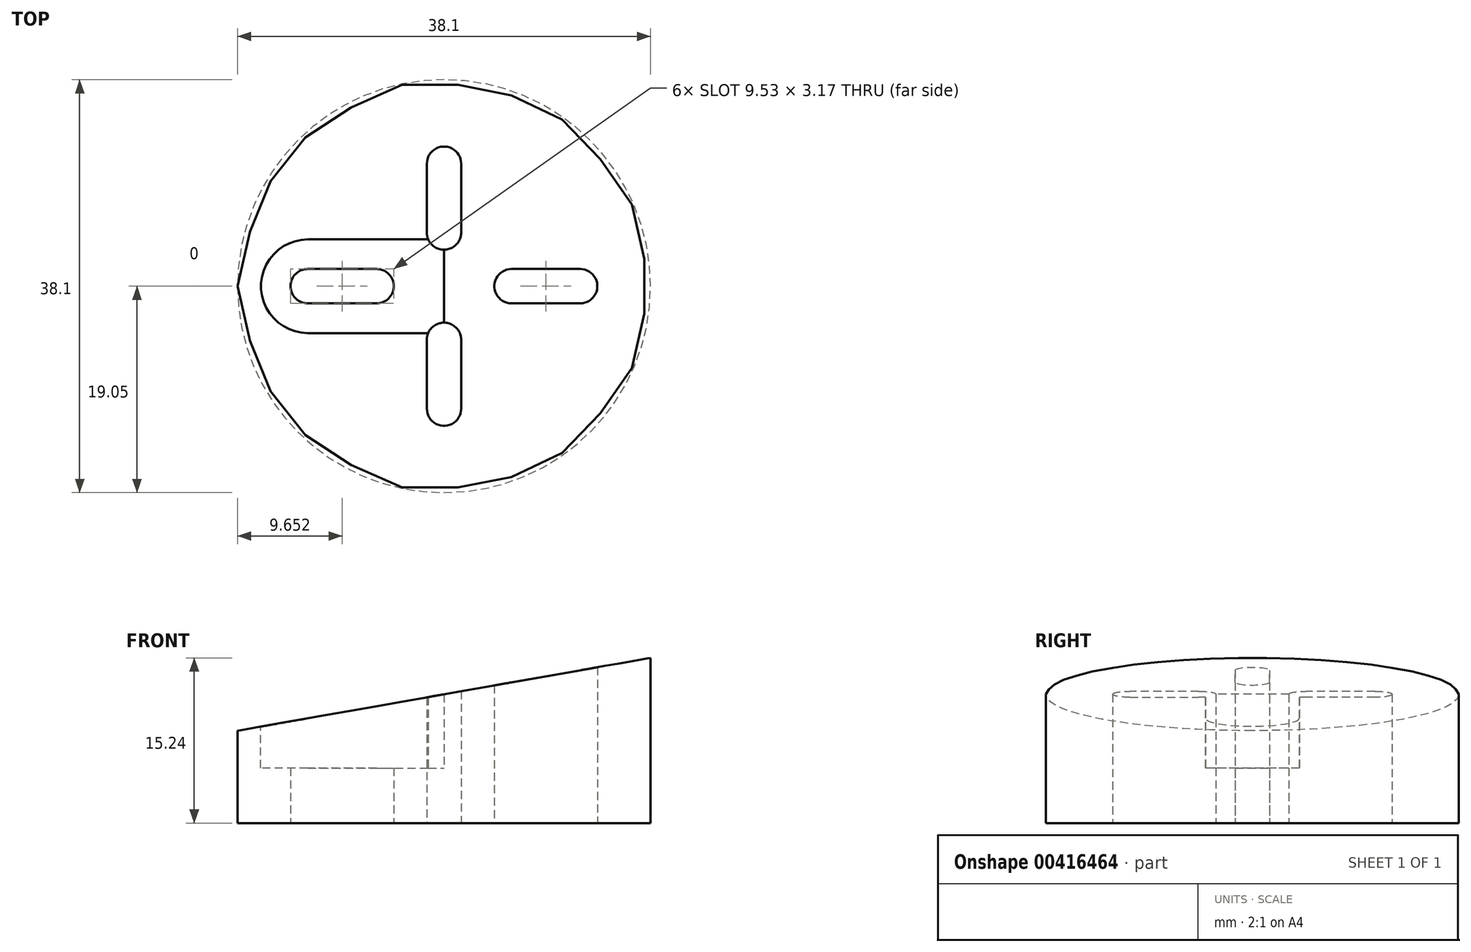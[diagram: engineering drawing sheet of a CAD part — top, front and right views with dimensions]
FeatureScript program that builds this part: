
annotation { "Feature Type Name" : "Feature", "Feature Type Description" : "" }
export const myFeature = defineFeature(function(context is Context, id is Id, definition is map)
    precondition{}
    {
        {
            var Q0;
            Q0=qCreatedBy(makeId("Top.planeOp"),FACE);
            var sketch = newSketch(context, id + "F0", { "sketchPlane" : qUnion([Q0])});
            skCircle(sketch, "E0", {"center": v(0, 0) * mm, "radius": 19.05 * mm});
            skSolve(sketch);
        }
        {
            var Q0;
            Q0 = qSketchRegion(id + "F0", true);
            extrude(context, id + "F1", {"entities" : qUnion([Q0]), "depth" : 25.4 * mm});
        }
        {
            var Q0;
            Q0=qCreatedBy(makeId("Front.planeOp"),FACE);
            var sketch = newSketch(context, id + "F2", { "sketchPlane" : qUnion([Q0])});
            skLineSegment(sketch, "E1", {"start": v(-19.05, 8.52) * mm, "end": v(19.05, 15.24) * mm});
            skLineSegment(sketch, "E2", {"start": v(19.05, 15.24) * mm, "end": v(19.05, 25.4) * mm});
            skLineSegment(sketch, "E3", {"start": v(19.05, 25.4) * mm, "end": v(-19.05, 25.4) * mm});
            skLineSegment(sketch, "E4", {"start": v(-19.05, 25.4) * mm, "end": v(-19.05, 8.52) * mm});
            skLineSegment(sketch, "E5", {"start": v(0, 0) * mm, "end": v(0, 25.4) * mm, "construction": true});
            skSolve(sketch);
        }
        {
            var Q0;
            Q0 = qSketchRegion(id + "F2", true);
            extrude(context, id + "F3", {"entities" : qUnion([Q0]), "operationType" : NewBodyOperationType.REMOVE, "endBound" : BoundingType.THROUGH_ALL, "depth" : 25.4 * mm, "hasSecondDirection" : true, "secondDirectionBound" : SecondDirectionBoundingType.THROUGH_ALL, "secondDirectionOppositeDirection" : true, "secondDirectionDepth" : 25.4 * mm});
        }
        {
            var Q0;
            Q0=qCreatedBy(makeId("Top.planeOp"),FACE);
            var sketch = newSketch(context, id + "F4", { "sketchPlane" : qUnion([Q0])});
            skLineSegment(sketch, "E6", {"start": v(0, -8.13) * mm, "end": v(0, 8.13) * mm, "construction": true});
            skLineSegment(sketch, "E7", {"start": v(-9.4, 0) * mm, "end": v(9.4, 0) * mm, "construction": true});
            skArc(sketch, "E8", {"start": v(-1.59, -11.3) * mm, "mid": v(0, -12.9) * mm, "end": v(1.59, -11.3) * mm});
            skArc(sketch, "E9", {"start": v(1.59, -4.95) * mm, "mid": v(0, -3.37) * mm, "end": v(-1.59, -4.95) * mm});
            skArc(sketch, "E10", {"start": v(-1.59, 4.95) * mm, "mid": v(0, 3.37) * mm, "end": v(1.59, 4.95) * mm});
            skArc(sketch, "E11", {"start": v(1.59, 11.3) * mm, "mid": v(0, 12.9) * mm, "end": v(-1.59, 11.3) * mm});
            skLineSegment(sketch, "E12", {"start": v(-1.59, 4.95) * mm, "end": v(-1.59, 11.3) * mm});
            skLineSegment(sketch, "E13", {"start": v(1.59, 4.95) * mm, "end": v(1.59, 11.3) * mm});
            skLineSegment(sketch, "E14", {"start": v(-1.59, -4.95) * mm, "end": v(-1.59, -11.3) * mm});
            skLineSegment(sketch, "E15", {"start": v(0, -11.3) * mm, "end": v(1.59, -11.3) * mm, "construction": true});
            skLineSegment(sketch, "E16", {"start": v(1.59, -11.3) * mm, "end": v(1.59, -4.95) * mm});
            skArc(sketch, "E17", {"start": v(6.22, 1.59) * mm, "mid": v(4.64, 0) * mm, "end": v(6.22, -1.59) * mm});
            skArc(sketch, "E18", {"start": v(12.57, -1.59) * mm, "mid": v(14.16, 0) * mm, "end": v(12.57, 1.59) * mm});
            skArc(sketch, "E19", {"start": v(-6.22, -1.59) * mm, "mid": v(-4.64, 0) * mm, "end": v(-6.22, 1.59) * mm});
            skArc(sketch, "E20", {"start": v(-12.57, 1.59) * mm, "mid": v(-14.16, 0) * mm, "end": v(-12.57, -1.59) * mm});
            skLineSegment(sketch, "E21", {"start": v(12.57, 1.59) * mm, "end": v(6.22, 1.59) * mm});
            skLineSegment(sketch, "E22", {"start": v(12.57, -1.59) * mm, "end": v(6.22, -1.59) * mm});
            skLineSegment(sketch, "E23", {"start": v(-6.22, 1.59) * mm, "end": v(-12.57, 1.59) * mm});
            skLineSegment(sketch, "E24", {"start": v(-6.22, -1.59) * mm, "end": v(-12.57, -1.59) * mm});
            skLineSegment(sketch, "E25", {"start": v(-12.57, -1.59) * mm, "end": v(-12.57, 0) * mm, "construction": true});
            skLineSegment(sketch, "E26", {"start": v(-6.22, 0) * mm, "end": v(-6.22, 1.59) * mm, "construction": true});
            skLineSegment(sketch, "E27.1.21", {"start": v(3.11, -5.39) * mm, "end": v(1.74, -6.18) * mm, "construction": true});
            skSolve(sketch);
        }
        {
            var Q0;
            Q0 = qSketchRegion(id + "F4", true);
            extrude(context, id + "F5", {"entities" : qUnion([Q0]), "operationType" : NewBodyOperationType.REMOVE, "endBound" : BoundingType.THROUGH_ALL, "depth" : 25.4 * mm});
        }
        {
            var Q0;
            Q0=qCreatedBy(makeId("Top.planeOp"),FACE);
            cPlane(context, id + "F6", {"entities" : qUnion([Q0]), "cplaneType" : CPlaneType.OFFSET, "offset" : 15.24 * mm, "width" : 152.4 * mm, "height" : 152.4 * mm});
        }
        {
            var Q0;
            Q0=qCreatedBy(id+"F6.planeOp",FACE);
            var sketch = newSketch(context, id + "F7", { "sketchPlane" : qUnion([Q0])});
            skLineSegment(sketch, "E28.0", {"start": v(-12.57, 1.59) * mm, "end": v(-6.22, 1.59) * mm, "construction": true});
            skArc(sketch, "E28.1", {"start": v(-12.57, -1.59) * mm, "mid": v(-14.16, 0) * mm, "end": v(-12.57, 1.59) * mm, "construction": true});
            skLineSegment(sketch, "E28.2", {"start": v(-12.57, -1.59) * mm, "end": v(-6.22, -1.59) * mm, "construction": true});
            skArc(sketch, "E28.3", {"start": v(-6.22, 1.59) * mm, "mid": v(-4.64, 0) * mm, "end": v(-6.22, -1.59) * mm, "construction": true});
            skLineSegment(sketch, "E29.0", {"start": v(-12.57, -4.33) * mm, "end": v(-6.22, -4.33) * mm});
            skArc(sketch, "E29.1", {"start": v(-12.57, -4.33) * mm, "mid": v(-16.9, 0) * mm, "end": v(-12.57, 4.33) * mm});
            skLineSegment(sketch, "E29.2", {"start": v(-12.57, 4.33) * mm, "end": v(-6.22, 4.33) * mm});
            skLineSegment(sketch, "E30", {"start": v(-6.22, 4.33) * mm, "end": v(0, 4.33) * mm});
            skLineSegment(sketch, "E31", {"start": v(0, 4.33) * mm, "end": v(0, -4.33) * mm});
            skLineSegment(sketch, "E32", {"start": v(0, -4.33) * mm, "end": v(-6.22, -4.33) * mm});
            skSolve(sketch);
        }
        {
            var Q0;
            Q0 = qSketchRegion(id + "F7", true);
            extrude(context, id + "F8", {"entities" : qUnion([Q0]), "operationType" : NewBodyOperationType.REMOVE, "oppositeDirection" : true, "depth" : 10.16 * mm});
        }
    });
